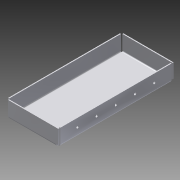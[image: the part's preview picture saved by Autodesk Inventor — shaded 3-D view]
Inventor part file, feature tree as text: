
AUTODESK INVENTOR PART (.ipt)
format: ipt  version: 2015 (Build 190159000, 159)  size: 232,448 bytes
history: native  units: in
note: dims shown in document units (in); Inventor stores cm internally (conversion verified against a paired STEP export)
features: sheet_metal_op x7, sketch x4, other x4, hole x1
ambient origin geometry x8: Origin, YZ Plane, XZ Plane, XY Plane, X Axis, Y Axis, Z Axis, Center Point
bodies: Solid1 (feature_tree)
feature tree (16):
  sheet_metal_op  "Face1"
  sheet_metal_op  "Flange1"
  sheet_metal_op  "Flange2"
  hole  "Hole2"  [1 undecoded]
  sketch  "Sketch1"  dims[d0=7.1in d1=3.2in]
  other  "Plate1"
  sketch  "Sketch3"  dims[d2=0.0625in]
  other  "Plate2"
  sheet_metal_op  "Bend1"
  sheet_metal_op  "Corner1"
  sketch  "Sketch4"  dims[d14=0.0625in]
  other  "Plate3"
  sheet_metal_op  "Bend2"
  sheet_metal_op  "Corner2"
  sketch  "Sketch5"  dims[d15=0.0312in d16=0.125in d17=0.0625in d18=1.0in d19=90.0deg d20=0.0625in d21=0.25in d22=0.0625in d23=0.0625in d24=0.0625in d25=0.0312in d26=0.125in d27=0.0625in d28=1.0in d29=90.0deg d30=0.0625in d31=0.25in d32=0.0625in d33=0.0625in d34=0.5in d35=0.1406in d36=0.339in d37=0.375in d38=0.25in d39=0.5635in d40=0.617in d41=0.8108in]
  other  "Definition1"
note: 1 required parameter value undecoded (feature->parameter linkage not recoverable at this tier; creation-order binding heuristic only, values carry confidence <= 0.55)
